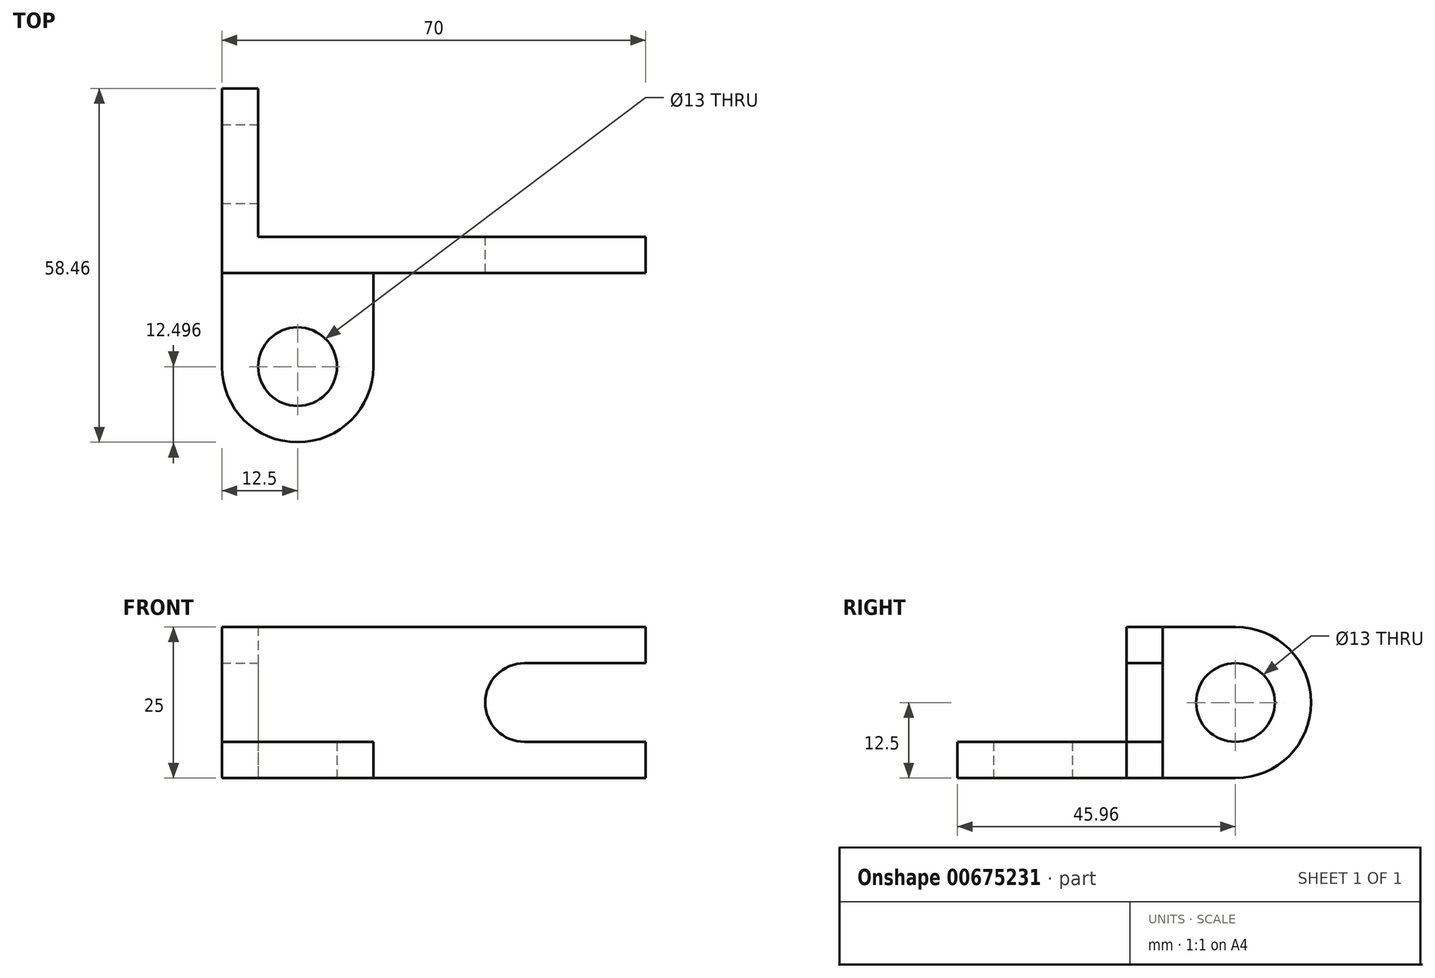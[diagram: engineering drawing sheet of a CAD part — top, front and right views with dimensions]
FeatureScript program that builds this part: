
annotation { "Feature Type Name" : "Feature", "Feature Type Description" : "" }
export const myFeature = defineFeature(function(context is Context, id is Id, definition is map)
    precondition{}
    {
        {
            var Q0;
            Q0=qCreatedBy(makeId("Front.planeOp"),FACE);
            var sketch = newSketch(context, id + "F0", { "sketchPlane" : qUnion([Q0])});
            skLineSegment(sketch, "E0.bottom", {"start": v(-32, 12.5) * mm, "end": v(32, 12.5) * mm});
            skLineSegment(sketch, "E0.top", {"start": v(-32, -12.5) * mm, "end": v(32, -12.5) * mm});
            skLineSegment(sketch, "E0.left", {"start": v(-32, 12.5) * mm, "end": v(-32, -12.5) * mm});
            skLineSegment(sketch, "E0.right", {"start": v(32, 12.5) * mm, "end": v(32, -12.5) * mm});
            skPoint(sketch, "E0.middle", {"position": v(0, 0) * mm});
            skLineSegment(sketch, "E1.bottom", {"start": v(12, 6.5) * mm, "end": v(32, 6.5) * mm});
            skLineSegment(sketch, "E1.top", {"start": v(12, -6.5) * mm, "end": v(32, -6.5) * mm});
            skLineSegment(sketch, "E1.left", {"start": v(12, 6.5) * mm, "end": v(12, -6.5) * mm});
            skLineSegment(sketch, "E1.right", {"start": v(32, 6.5) * mm, "end": v(32, -6.5) * mm});
            skPoint(sketch, "E1.middle", {"position": v(22, 0) * mm});
            skCircle(sketch, "E2", {"center": v(12, 0) * mm, "radius": 6.5 * mm});
            skSolve(sketch);
        }
        {
            var Q0;
            {var subQ1=sQuery(id+"F0.wireOp",EDGE,"E0.bottom");Q0=makeQuery(id+"F0.imprint","IMPRINT",FACE,{"disambiguationData":[TD([[makeQuery(id+"F0.imprint","IMPRINT",EDGE,{"derivedFrom":subQ1}),-1.0]])]});}
            extrude(context, id + "F1", {"entities" : qUnion([Q0]), "depth" : 6 * mm, "offsetDistance" : 25 * mm});
        }
        {
            var Q0;
            Q0=makeQuery(id+"F1.opExtrude","SWEPT_FACE",FACE,{"disambiguationData":[OSD([sQuery(id+"F0.wireOp",EDGE,"E0.left")])]});
            var sketch = newSketch(context, id + "F2", { "sketchPlane" : qUnion([Q0])});
            skLineSegment(sketch, "E3.bottom", {"start": v(6, 12.5) * mm, "end": v(-12, 12.5) * mm});
            skLineSegment(sketch, "E3.top", {"start": v(6, -12.5) * mm, "end": v(-12, -12.5) * mm});
            skLineSegment(sketch, "E3.left", {"start": v(6, 12.5) * mm, "end": v(6, -12.5) * mm});
            skLineSegment(sketch, "E3.right", {"start": v(-12, 12.5) * mm, "end": v(-12, 6.5) * mm});
            skCircle(sketch, "E4", {"center": v(-12, 0) * mm, "radius": 12.5 * mm});
            skCircle(sketch, "E5", {"center": v(-12, 0) * mm, "radius": 6.5 * mm});
            skLineSegment(sketch, "E6.trimOffspring", {"start": v(-12, -6.5) * mm, "end": v(-12, -12.5) * mm});
            skSolve(sketch);
        }
        {
            var Q0;
            Q0 = qSketchRegion(id + "F2", true);
            extrude(context, id + "F3", {"entities" : qUnion([Q0]), "operationType" : NewBodyOperationType.ADD, "depth" : 6 * mm, "offsetDistance" : 25 * mm});
        }
        {
            var Q0;
            Q0=makeQuery(id+"F3.boolean.opBoolean","MERGE",FACE,{"derivedFrom":[makeQuery(id+"F1.opExtrude","SWEPT_FACE",FACE,{"disambiguationData":[OSD([sQuery(id+"F0.wireOp",EDGE,"E0.top")])]}),makeQuery(id+"F3.opExtrude","SWEPT_FACE",FACE,{"disambiguationData":[OSD([sQuery(id+"F2.wireOp",EDGE,"E3.top")])]})]});
            var sketch = newSketch(context, id + "F4", { "sketchPlane" : qUnion([Q0])});
            skLineSegment(sketch, "E7.bottom", {"start": v(-38, 0) * mm, "end": v(-13, 0) * mm});
            skLineSegment(sketch, "E7.top", {"start": v(-38, 21.46) * mm, "end": v(-13, 21.46) * mm});
            skLineSegment(sketch, "E7.left", {"start": v(-38, 0) * mm, "end": v(-38, 21.46) * mm});
            skLineSegment(sketch, "E7.right", {"start": v(-13, 0) * mm, "end": v(-13, 21.46) * mm});
            skCircle(sketch, "E8", {"center": v(-25.5, 21.46) * mm, "radius": 12.5 * mm});
            skCircle(sketch, "E9", {"center": v(-25.5, 21.46) * mm, "radius": 6.5 * mm});
            skSolve(sketch);
        }
        {
            var Q0;
            {var subQ1=sQuery(id+"F4.wireOp",EDGE,"E7.top");var subQ3=sQuery(id+"F4.wireOp",EDGE,"E9");var subQ4=makeQuery(id+"F4.imprint","INTERSECT",VERTEX,{"disambiguationData":[OD(0.0)],"derivedFrom":[subQ1,subQ3]});Q0=makeQuery(id+"F4.imprint","IMPRINT",FACE,{"disambiguationData":[TD([[makeQuery(id+"F4.imprint","IMPRINT",EDGE,{"disambiguationData":[TD([[subQ4,1.0]])],"derivedFrom":subQ3}),-1.0]])]});}
            var Q1;
            {var subQ1=sQuery(id+"F4.wireOp",EDGE,"E7.top");var subQ3=sQuery(id+"F4.wireOp",EDGE,"E9");var subQ4=makeQuery(id+"F4.imprint","INTERSECT",VERTEX,{"disambiguationData":[OD(0.0)],"derivedFrom":[subQ1,subQ3]});Q1=makeQuery(id+"F4.imprint","IMPRINT",FACE,{"disambiguationData":[TD([[makeQuery(id+"F4.imprint","IMPRINT",EDGE,{"disambiguationData":[TD([[subQ4,-1.0]])],"derivedFrom":subQ3}),-1.0]])]});}
            var Q2;
            {var subQ1=sQuery(id+"F4.wireOp",EDGE,"E7.bottom");var subQ4=sQuery(id+"F2.wireOp",EDGE,"E3.top");var subQ7=makeQuery(id+"F4.imprint","INTERSECT",VERTEX,{"derivedFrom":[makeQuery(id+"F3.opExtrude","CAP_EDGE",EDGE,{"disambiguationData":[OSD([subQ4])],"isStart":true}),subQ1]});Q2=makeQuery(id+"F4.imprint","IMPRINT",FACE,{"disambiguationData":[TD([[makeQuery(id+"F4.imprint","IMPRINT",EDGE,{"disambiguationData":[TD([[subQ7,-1.0]])],"derivedFrom":subQ1}),1.0]])]});}
            var Q3;
            {var subQ0=sQuery(id+"F4.wireOp",EDGE,"E7.left");var subQ3=sQuery(id+"F4.wireOp",EDGE,"E8");var subQ4=sQuery(id+"F4.wireOp",EDGE,"E7.top");var subQ5=makeQuery(id+"F4.imprint","INTERSECT",VERTEX,{"derivedFrom":[subQ4,subQ0,subQ3]});Q3=makeQuery(id+"F4.imprint","IMPRINT",FACE,{"disambiguationData":[TD([[makeQuery(id+"F4.imprint","IMPRINT",EDGE,{"disambiguationData":[TD([[subQ5,-1.0]])],"derivedFrom":subQ3}),-1.0]])]});}
            extrude(context, id + "F5", {"entities" : qUnion([Q0, Q1, Q2, Q3]), "operationType" : NewBodyOperationType.ADD, "oppositeDirection" : true, "depth" : 6 * mm, "offsetDistance" : 25 * mm});
        }
    });
